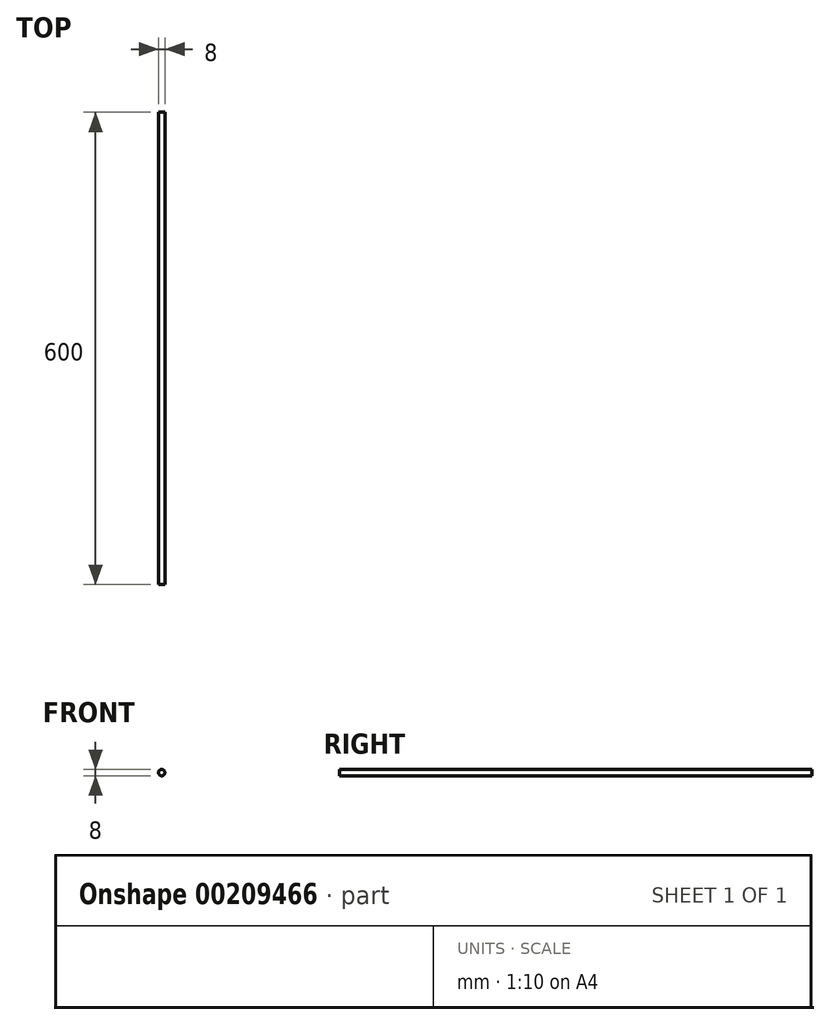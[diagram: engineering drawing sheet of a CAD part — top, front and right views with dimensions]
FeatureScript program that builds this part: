
annotation { "Feature Type Name" : "Feature", "Feature Type Description" : "" }
export const myFeature = defineFeature(function(context is Context, id is Id, definition is map)
    precondition{}
    {
        {
            var Q0;
            Q0=qCreatedBy(makeId("Front.planeOp"),FACE);
            var sketch = newSketch(context, id + "F0", { "sketchPlane" : qUnion([Q0])});
            skCircle(sketch, "E0", {"center": v(0, 0) * mm, "radius": 4 * mm});
            skSolve(sketch);
        }
        {
            var Q0;
            Q0 = qSketchRegion(id + "F0", true);
            extrude(context, id + "F1", {"entities" : qUnion([Q0]), "depth" : 600 * mm});
        }
    });
